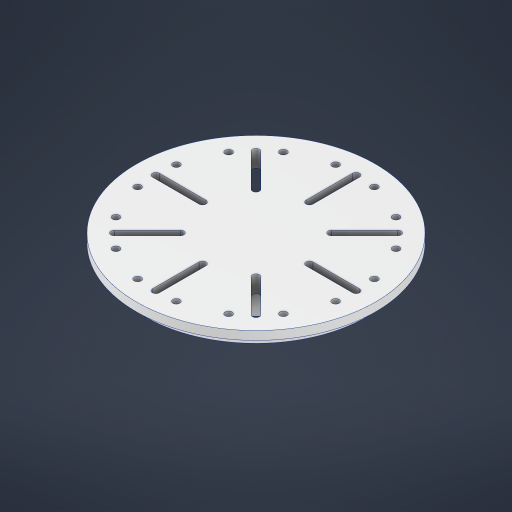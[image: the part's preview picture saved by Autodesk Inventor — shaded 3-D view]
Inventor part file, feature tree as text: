
AUTODESK INVENTOR PART (.ipt)
format: ipt  version: 2024 (Build 280153000, 153)  size: 248,832 bytes
history: native  units: mm
features: extrude x3, sketch x3, pattern_circular x1, chamfer x1
ambient origin geometry x8: Origin, YZ Plane, XZ Plane, XY Plane, X Axis, Y Axis, Z Axis, Center Point
bodies: Solid1 (feature_tree)
feature tree (8):
  extrude  "Extrusion1"  Depth=40.0mm TaperAngle=0.0deg
  extrude  "Extrusion2"  Depth=30.0mm TaperAngle=0.0deg
  extrude  "Extrusion3"  Depth=80.0mm TaperAngle=360.0deg
  pattern_circular  "Circular Pattern1"  Angle=45.0deg  [1 undecoded]
  chamfer  "Chamfer1"  [1 undecoded]
  sketch  "Sketch1"  dims[d0=160.0mm d1=40.0mm d2=0.0mm]
  sketch  "Sketch2"  dims[d3=420.0mm d4=30.0mm d5=0.0mm]
  sketch  "Sketch3"  dims[d6=30.0mm d7=0.0mm d8=80.0mm d9=360.0deg d11=15.0mm d12=2.0mm d13=45.0deg]
note: 2 required parameter values undecoded (feature->parameter linkage not recoverable at this tier; creation-order binding heuristic only, values carry confidence <= 0.55)
